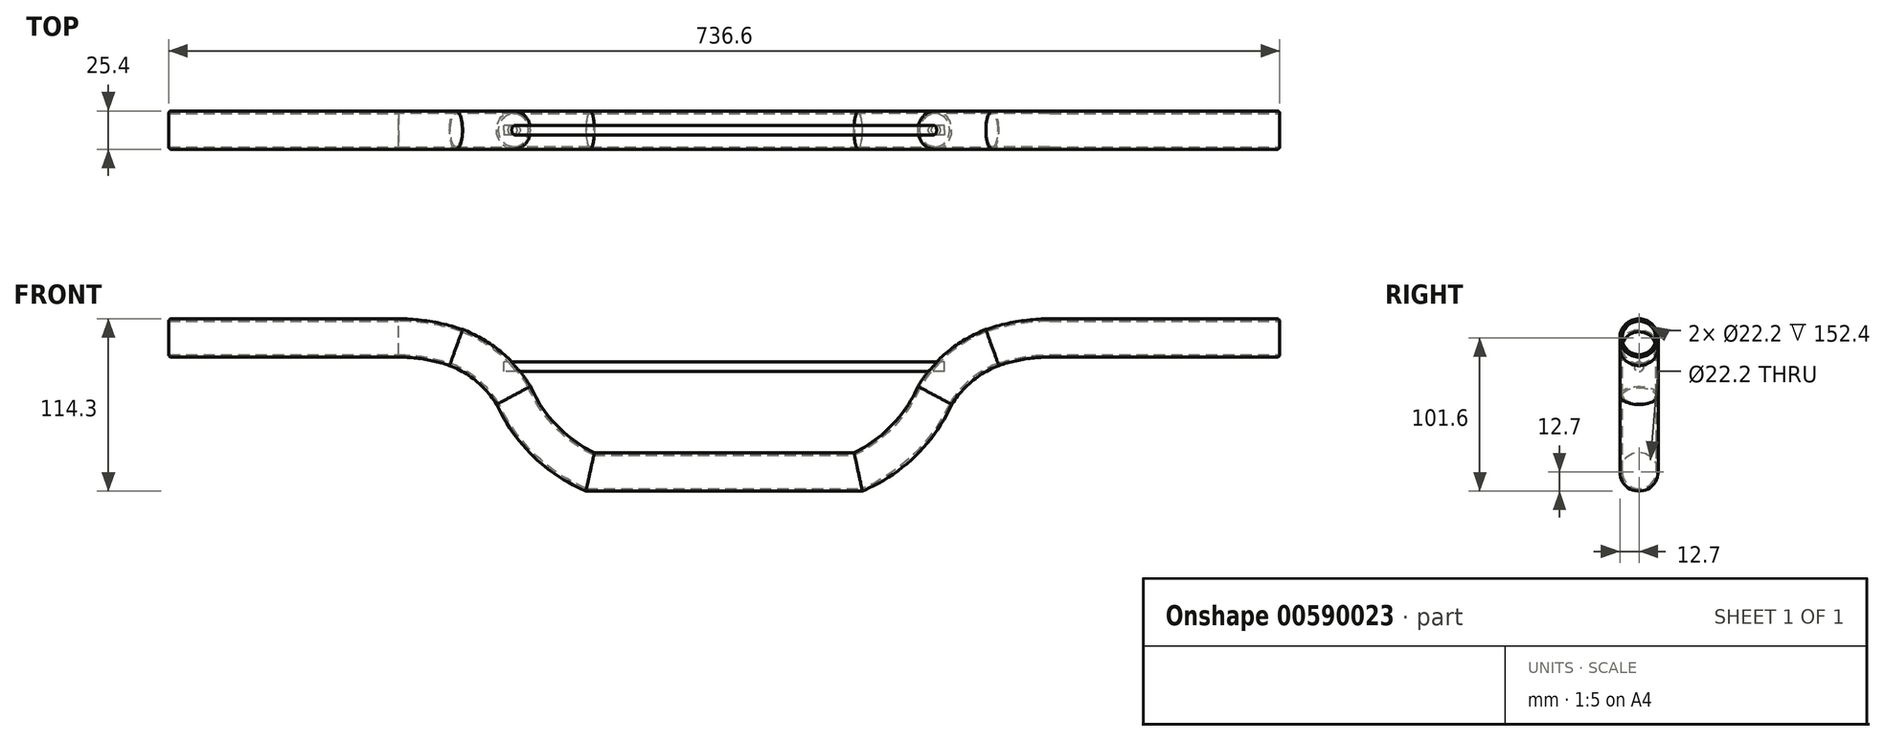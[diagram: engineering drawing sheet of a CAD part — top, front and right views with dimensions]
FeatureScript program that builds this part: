
annotation { "Feature Type Name" : "Feature", "Feature Type Description" : "" }
export const myFeature = defineFeature(function(context is Context, id is Id, definition is map)
    precondition{}
    {
        {
            var Q0;
            Q0=qCreatedBy(makeId("Right.planeOp"),FACE);
            var sketch = newSketch(context, id + "F0", { "sketchPlane" : qUnion([Q0])});
            skCircle(sketch, "E0", {"center": v(0, 0) * mm, "radius": 12.7 * mm});
            skSolve(sketch);
        }
        {
            var Q0;
            Q0=qCreatedBy(makeId("Front.planeOp"),FACE);
            var sketch = newSketch(context, id + "F1", { "sketchPlane" : qUnion([Q0])});
            skLineSegment(sketch, "E1", {"start": v(0, 0) * mm, "end": v(152.4, 0) * mm});
            skArc(sketch, "E2", {"start": v(190.5, -6.35) * mm, "mid": v(171.71, -1.6) * mm, "end": v(152.4, 0) * mm});
            skArc(sketch, "E3", {"start": v(228.6, -38.1) * mm, "mid": v(212.2, -19.04) * mm, "end": v(190.5, -6.35) * mm});
            skArc(sketch, "E4", {"start": v(228.6, -38.1) * mm, "mid": v(249.36, -68.14) * mm, "end": v(279.4, -88.9) * mm});
            skArc(sketch, "E5", {"start": v(457.2, -88.9) * mm, "mid": v(487.24, -68.14) * mm, "end": v(508, -38.1) * mm});
            skArc(sketch, "E6", {"start": v(546.1, -6.35) * mm, "mid": v(524.4, -19.04) * mm, "end": v(508, -38.1) * mm});
            skArc(sketch, "E7", {"start": v(584.2, 0) * mm, "mid": v(564.89, -1.6) * mm, "end": v(546.1, -6.35) * mm});
            skLineSegment(sketch, "E8", {"start": v(584.2, 0) * mm, "end": v(736.6, 0) * mm});
            skLineSegment(sketch, "E9", {"start": v(279.4, -88.9) * mm, "end": v(457.2, -88.9) * mm});
            skSolve(sketch);
        }
        {
            var Q0;
            Q0 = qSketchRegion(id + "F0", true);
            var Q1;
            Q1 = qConstructionFilter(qBodyType(qCreatedBy(id + "F1" ,EDGE), BodyType.WIRE), ConstructionObject.NO);
            sweep(context, id + "F2", {"profiles" : qUnion([Q0]), "path" : qUnion([Q1])});
        }
        {
            var Q0;
            Q0=makeQuery(id+"F2.opSweep","CAP_FACE",FACE,{"disambiguationData":[OSD([sQuery(id+"F0.wireOp",EDGE,"E0"),sQuery(id+"F1.wireOp",VERTEX,"E1.start")])],"isStart":true});
            var Q1;
            Q1=makeQuery(id+"F2.opSweep","CAP_FACE",FACE,{"disambiguationData":[OSD([sQuery(id+"F0.wireOp",EDGE,"E0"),sQuery(id+"F1.wireOp",VERTEX,"E8.end")])],"isStart":false});
            shell(context, id + "F3", {"entities" : qUnion([Q0, Q1]), "thickness" : 1.6 * mm});
        }
        {
            var Q0;
            Q0=makeQuery(id+"F2.opSweep","CAP_EDGE",EDGE,{"disambiguationData":[OSD([sQuery(id+"F0.wireOp",EDGE,"E0"),sQuery(id+"F1.wireOp",VERTEX,"E1.start")])],"isStart":true});
            var Q1;
            Q1=makeQuery(id+"F2.opSweep","CAP_EDGE",EDGE,{"disambiguationData":[OSD([sQuery(id+"F0.wireOp",EDGE,"E0"),sQuery(id+"F1.wireOp",VERTEX,"E8.end")])],"isStart":false});
            fillet(context, id + "F4", {"entities" : qUnion([Q0, Q1]), "radius" : 1.59 * mm, "tangentPropagation" : true, "allowEdgeOverflow" : false});
        }
        {
            var Q0;
            Q0=qCreatedBy(makeId("Right.planeOp"),FACE);
            cPlane(context, id + "F5", {"entities" : qUnion([Q0]), "cplaneType" : CPlaneType.OFFSET, "offset" : 222.25 * mm, "width" : 152.4 * mm, "height" : 152.4 * mm});
        }
        {
            var Q0;
            Q0=qCreatedBy(id+"F5.planeOp",FACE);
            var sketch = newSketch(context, id + "F6", { "sketchPlane" : qUnion([Q0])});
            skCircle(sketch, "E10", {"center": v(0, -19.05) * mm, "radius": 3.18 * mm});
            skSolve(sketch);
        }
        {
            var Q0;
            Q0 = qSketchRegion(id + "F6", true);
            extrude(context, id + "F7", {"entities" : qUnion([Q0]), "operationType" : NewBodyOperationType.ADD, "depth" : 292.1 * mm, "offsetDistance" : 25.4 * mm});
        }
    });
